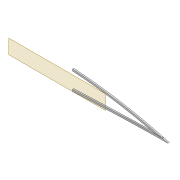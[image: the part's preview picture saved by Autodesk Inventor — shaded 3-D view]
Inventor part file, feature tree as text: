
AUTODESK INVENTOR PART (.ipt)
format: ipt  version: 2022 (Build 260153000, 153)  size: 421,376 bytes
history: native  units: mm
features: extrude x8, sketch x7, projected_geometry x6, fillet x2, shell x1, plane x1
ambient origin geometry x8: Origin, YZ Plane, XZ Plane, XY Plane, X Axis, Y Axis, Z Axis, Center Point
bodies: Solid1 (feature_tree)
feature tree (25):
  extrude  "Extrusion1"  Depth=5.0mm
  shell  "Shell1"  Thickness=2.0mm
  extrude  "Extrusion8"  Depth=5.9mm
  extrude  "Extrusion3"  Depth=10.0mm TaperAngle=0.0deg
  extrude  "Extrusion4"  Depth=2.0mm
  fillet  "Fillet1"  Radius=5.0mm
  sketch  "Sketch10"  dims[d22=4.0mm d23=0.0mm d31=2.0mm d32=5.0mm]
  extrude  "Extrusion5"  Depth=2.5mm
  plane  "Work Plane2"
  extrude  "Extrusion9"  Depth=1.6mm
  fillet  "Fillet2"  Radius=2.5mm
  extrude  "Extrusion10"  Depth=6.0mm
  extrude  "Extrusion11"  Depth=4.0mm TaperAngle=0.0deg
  sketch  "Sketch3"  dims[d0=4.0mm d1=0.0mm d2=5.0mm d7=2.0mm]
  sketch  "Sketch8"  dims[d8=2.0mm d9=5.9mm]
  sketch  "Sketch9"  dims[d13=10.0mm d14=0.0mm d16=10.0mm d17=0.0mm]
  projected_geometry  "Projected Loop4"
  projected_geometry  "Projected Loop10"
  sketch  "Sketch24"  dims[d34=1.6mm d35=2.5mm]
  projected_geometry  "Projected Loop11"
  projected_geometry  "Projected Loop12"
  projected_geometry  "Projected Loop13"
  sketch  "Sketch26"  dims[d37=5.0mm d38=1.6mm d40=2.5mm]
  projected_geometry  "Projected Loop14"
  sketch  "Sketch27"  dims[d62=80.0mm d63=6.0mm d64=4.0mm d65=0.0mm d66=3.0mm d67=12.0mm d68=5.0mm d69=10.0mm d70=12.0mm d71=3.05mm d72=10.0mm d73=0.0mm d74=2.0mm d75=100.0mm d76=20.0mm d77=0.5mm d78=10.0mm d79=0.0mm d80=10.0mm d81=0.0mm]
